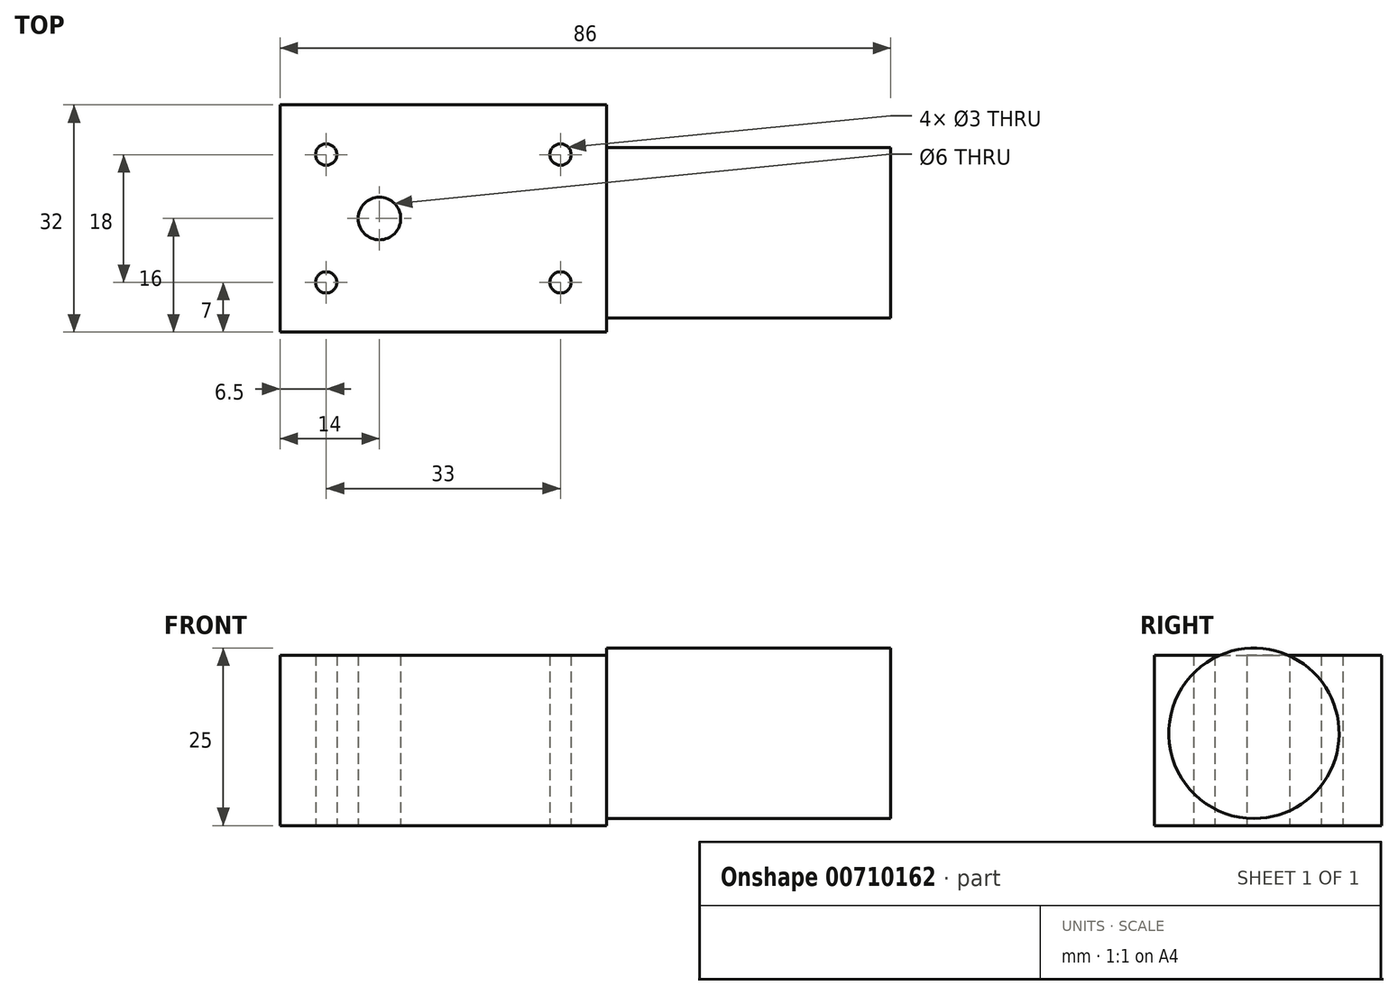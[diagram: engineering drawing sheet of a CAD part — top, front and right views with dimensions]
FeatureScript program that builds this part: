
annotation { "Feature Type Name" : "Feature", "Feature Type Description" : "" }
export const myFeature = defineFeature(function(context is Context, id is Id, definition is map)
    precondition{}
    {
        {
            var Q0;
            Q0=qCreatedBy(makeId("Top.planeOp"),FACE);
            var sketch = newSketch(context, id + "F0", { "sketchPlane" : qUnion([Q0])});
            skLineSegment(sketch, "E0.bottom", {"start": v(16.5, -9) * mm, "end": v(-16.5, -9) * mm, "construction": true});
            skLineSegment(sketch, "E0.top", {"start": v(16.5, 9) * mm, "end": v(-16.5, 9) * mm, "construction": true});
            skLineSegment(sketch, "E0.left", {"start": v(16.5, -9) * mm, "end": v(16.5, 9) * mm, "construction": true});
            skLineSegment(sketch, "E0.right", {"start": v(-16.5, -9) * mm, "end": v(-16.5, 9) * mm, "construction": true});
            skPoint(sketch, "E0.middle", {"position": v(0, 0) * mm});
            skCircle(sketch, "E1", {"center": v(-16.5, 9) * mm, "radius": 1.5 * mm});
            skCircle(sketch, "E2", {"center": v(16.5, 9) * mm, "radius": 1.5 * mm});
            skCircle(sketch, "E3", {"center": v(16.5, -9) * mm, "radius": 1.5 * mm});
            skCircle(sketch, "E4", {"center": v(-16.5, -9) * mm, "radius": 1.5 * mm});
            skLineSegment(sketch, "E5.bottom", {"start": v(23, -16) * mm, "end": v(-23, -16) * mm});
            skLineSegment(sketch, "E5.top", {"start": v(23, 16) * mm, "end": v(-23, 16) * mm});
            skLineSegment(sketch, "E5.left", {"start": v(23, -16) * mm, "end": v(23, 16) * mm});
            skLineSegment(sketch, "E5.right", {"start": v(-23, -16) * mm, "end": v(-23, 16) * mm});
            skCircle(sketch, "E6", {"center": v(-9, 0) * mm, "radius": 3 * mm});
            skSolve(sketch);
        }
        {
            var Q0;
            Q0=makeQuery(id+"F0.imprint","IMPRINT",FACE,{"disambiguationData":[TD([[makeQuery(id+"F0.imprint","IMPRINT",EDGE,{"derivedFrom":sQuery(id+"F0.wireOp",EDGE,"E1")}),-1.0]])]});
            extrude(context, id + "F1", {"entities" : qUnion([Q0]), "depth" : 24 * mm, "offsetDistance" : 25 * mm});
        }
        {
            var Q0;
            Q0=makeQuery(id+"F1.opExtrude","SWEPT_FACE",FACE,{"disambiguationData":[OSD([sQuery(id+"F0.wireOp",EDGE,"E5.left")])]});
            var sketch = newSketch(context, id + "F2", { "sketchPlane" : qUnion([Q0])});
            skLineSegment(sketch, "E7.bottom", {"start": v(0, 0) * mm, "end": v(-2, 0) * mm, "construction": true});
            skLineSegment(sketch, "E7.top", {"start": v(0, 13) * mm, "end": v(-2, 13) * mm, "construction": true});
            skLineSegment(sketch, "E7.left", {"start": v(0, 0) * mm, "end": v(0, 13) * mm, "construction": true});
            skLineSegment(sketch, "E7.right", {"start": v(-2, 0) * mm, "end": v(-2, 13) * mm, "construction": true});
            skCircle(sketch, "E8", {"center": v(-2, 13) * mm, "radius": 12 * mm});
            skSolve(sketch);
        }
        {
            var Q0;
            {var subQ0=sQuery(id+"F2.wireOp",EDGE,"E8");var subQ1=makeQuery(id+"F1.opExtrude","CAP_EDGE",EDGE,{"disambiguationData":[OSD([sQuery(id+"F0.wireOp",EDGE,"E5.left")])],"isStart":false});var subQ2=makeQuery(id+"F2.imprint","INTERSECT",VERTEX,{"disambiguationData":[OD(0.0)],"derivedFrom":[subQ1,subQ0]});Q0=makeQuery(id+"F2.imprint","IMPRINT",FACE,{"disambiguationData":[TD([[makeQuery(id+"F2.imprint","IMPRINT",EDGE,{"disambiguationData":[TD([[subQ2,-1.0]])],"derivedFrom":subQ0}),1.0]])]});}
            var Q1;
            {var subQ0=sQuery(id+"F2.wireOp",EDGE,"E8");var subQ1=makeQuery(id+"F1.opExtrude","CAP_EDGE",EDGE,{"disambiguationData":[OSD([sQuery(id+"F0.wireOp",EDGE,"E5.left")])],"isStart":false});var subQ2=makeQuery(id+"F2.imprint","INTERSECT",VERTEX,{"disambiguationData":[OD(0.0)],"derivedFrom":[subQ1,subQ0]});Q1=makeQuery(id+"F2.imprint","IMPRINT",FACE,{"disambiguationData":[TD([[makeQuery(id+"F2.imprint","IMPRINT",EDGE,{"disambiguationData":[TD([[subQ2,1.0]])],"derivedFrom":subQ0}),1.0]])]});}
            extrude(context, id + "F3", {"entities" : qUnion([Q0, Q1]), "operationType" : NewBodyOperationType.ADD, "depth" : 40 * mm, "offsetDistance" : 25 * mm});
        }
    });
